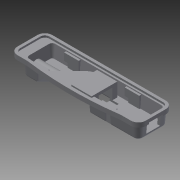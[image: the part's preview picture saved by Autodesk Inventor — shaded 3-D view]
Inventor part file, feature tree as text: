
AUTODESK INVENTOR PART (.ipt)
format: ipt  version: 2014 (Build 180170000, 170)  size: 471,552 bytes
history: native  units: mm
features: sketch x12, extrude x11, fillet x2, sweep x1, shell x1
ambient origin geometry x8: Origin, YZ Plane, XZ Plane, XY Plane, X Axis, Y Axis, Z Axis, Center Point
bodies: Solid1 (feature_tree)
feature tree (27):
  extrude  "Extrusion1"  Depth=38.0mm
  extrude  "Extrusion2"  Depth=70.0mm
  extrude  "Extrusion4"  Depth=8.0mm
  extrude  "Extrusion5"  Depth=3.5mm
  extrude  "Extrusion6"  Depth=30.0mm
  sweep  "Sweep1"
  extrude  "Extrusion7"  Depth=15.0mm
  extrude  "Extrusion8"  Depth=18.0mm
  extrude  "Extrusion12"  Depth=2.0mm
  shell  "Shell1"  Thickness=2.0mm
  extrude  "Extrusion9"  Depth=10.0mm
  extrude  "Extrusion10"  Depth=13.5mm
  extrude  "Extrusion11"  Depth=16.0mm
  fillet  "Fillet3"  Radius=9.0mm
  fillet  "Fillet4"  Radius=3.0mm
  sketch  "Sketch2"  dims[d0=19.0mm d1=38.0mm]
  sketch  "Sketch4"  dims[d2=140.0mm d3=70.0mm]
  sketch  "Sketch5"  dims[d4=8.0mm d5=8.0mm]
  sketch  "Sketch6"  dims[d6=5.0mm d7=0.0mm d12=3.5mm]
  sketch  "Sketch7"  dims[d17=5.0mm d18=0.0mm d24=30.0mm]
  sketch  "Sketch8"  dims[d25=30.0mm d26=18.0mm]
  sketch  "Sketch9"  dims[d27=15.0mm d28=15.0mm]
  sketch  "Sketch10"  dims[d30=2.0mm d31=18.0mm]
  sketch  "Sketch11"  dims[d32=5.5mm d33=2.0mm d34=2.0mm]
  sketch  "Sketch12"  dims[d35=2.0mm d36=10.0mm]
  sketch  "Sketch13"  dims[d37=6.0mm d38=13.5mm d39=-0.872665mm]
  sketch  "Sketch14"  dims[d41=54.0mm d42=16.0mm d43=9.0mm d44=3.0mm d45=15.0mm d46=0.0mm d47=0.0mm d48=0.0mm d50=45.0deg d51=15.0mm d52=25.0mm d53=12.5mm d54=0.0mm d55=0.0mm d56=45.0deg d57=0.0mm d58=0.0mm d59=20.0mm d60=0.0mm d61=15.0mm d63=33.0mm d64=6.1mm d65=6.1mm d66=10.0mm d67=10.0mm d68=2.0mm d69=2.0mm d70=1.0mm d71=1.0mm d74=60.0mm d75=4.0mm d76=0.0mm d77=6.0mm d78=6.0mm d79=2.0mm d80=2.0mm d81=1.0mm d82=1.0mm d83=0.0mm d85=33.0mm d86=10.0mm d87=10.0mm d88=64.0mm d89=4.0mm d90=0.0mm d91=1.5mm d92=15.0mm d93=7.5mm d94=12.0mm d95=10.0mm d96=0.0mm d97=15.0mm d98=3.0mm d99=14.0mm d100=0.0mm d101=10.0mm d102=0.0mm d103=3.0mm d105=5.0mm d107=5.0mm d108=5.0mm d109=2.0mm d110=0.5mm d111=2.0mm d112=2.0mm d113=12.0mm d114=6.0mm d115=2.0mm d116=0.0mm d117=2.5mm d118=7.0mm d119=10.0mm d120=13.0mm d121=50.0mm d122=0.0mm]
